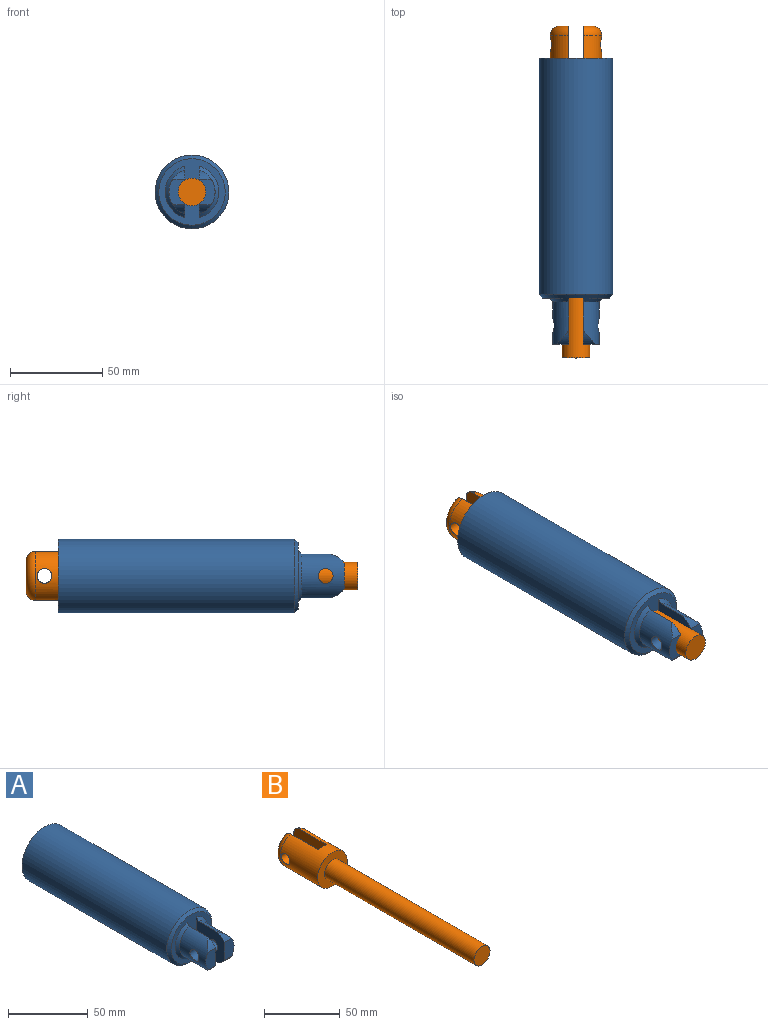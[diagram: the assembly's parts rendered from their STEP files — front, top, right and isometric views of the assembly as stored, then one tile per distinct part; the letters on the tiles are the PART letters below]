
ASSEMBLY  parts=2 mates=1
PART A: 20 faces, bbox 40x155x40 mm
  f0: cylinder r=12.5mm len=23.69mm, axis (0,1,0), area 611mm2, adj f1,f2,f12,f14,f18,f19
  f1: plane 27.92x25.05mm, normal (-1,0,0), area 519mm2, adj f0,f2,f6,f12,f14,f18,f19
  f2: plane 13.64x8.5mm, normal (0,-1,0), area 107mm2, adj f0,f1,f18,f19
  f3: plane 27.92x25.05mm, normal (1,0,0), area 519mm2, adj f4,f5,f6,f11,f13,f16,f17
  f4: cylinder r=12.5mm len=23.69mm, axis (0,1,0), area 610.9mm2, adj f3,f5,f11,f13,f16,f17
  f5: plane 13.64x8.5mm, normal (0,-1,0), area 107mm2, adj f3,f4,f16,f17
  f6: plane 36x36mm, normal (0,-1,0), area 586.4mm2, adj f1,f3,f13,f14,f15
  f7: cylinder r=7.5mm len=120mm, axis (0,1,0), area 5654.9mm2, adj f9,f10
  f8: cylinder r=20mm len=128mm, axis (0,1,0), area 16085mm2, adj f9,f15
  f9: plane 40x40mm, normal (0,1,0), area 1079.9mm2, adj f7,f8
  f10: plane 15x15mm, normal (0,1,0), area 176.7mm2, adj f7
  f11: cylinder r=4mm len=8.5mm, axis (1,0,0), area 205.4mm2, adj f3,f4
  f12: cylinder r=4mm len=8.5mm, axis (1,0,0), area 205.4mm2, adj f0,f1
  f13: cone r=12.5mm half-angle=45deg, axis (0,1,0), area 96.9mm2, adj f3,f4,f6
  f14: cone r=12.5mm half-angle=45deg, axis (0,1,0), area 96.9mm2, adj f0,f1,f6
  f15: cone r=18mm half-angle=45deg, axis (0,1,0), area 337.7mm2, adj f6,f8
  f16: cylinder r=12.1mm len=7.5mm, axis (1,0,0), area 31mm2, adj f3,f4,f5
  f17: cylinder r=12.1mm len=7.5mm, axis (1,0,0), area 31mm2, adj f3,f4,f5
  f18: cylinder r=12.1mm len=7.5mm, axis (1,0,0), area 31mm2, adj f0,f1,f2
  f19: cylinder r=12.1mm len=7.5mm, axis (1,0,0), area 31mm2, adj f0,f1,f2
PART B: 13 faces, bbox 30x180x28.7 mm
  f0: plane 15.82x4.86mm, normal (0,1,0), area 55mm2, adj f2,f9
  f1: cylinder r=13.86mm len=35mm, axis (0,1,0), area 2525.8mm2, adj f2,f6,f7,f8,f9,f10,f11,f12
  f2: torus R=8.86mm, axis (0,-1,0), area 233.1mm2, adj f0,f1,f9
  f3: cylinder r=7.5mm len=140mm, axis (0,-1,0), area 6597.3mm2, adj f4,f6
  f4: plane 15x15mm, normal (0,-1,0), area 176.7mm2, adj f3
  f5: plane 15.82x4.86mm, normal (0,1,0), area 55mm2, adj f7,f10
  f6: plane 27.72x27.72mm, normal (0,-1,0), area 427mm2, adj f1,f3
  f7: torus R=8.86mm, axis (0,-1,0), area 233.1mm2, adj f1,f5,f10
  f8: cylinder r=25mm len=27.73mm, axis (1,0,0), area 231.4mm2, adj f1,f9,f10
  f9: plane 35x26.55mm, normal (1,0,0), area 834.9mm2, adj f0,f1,f2,f8,f12
  f10: plane 35x26.55mm, normal (-1,0,0), area 834.9mm2, adj f1,f5,f7,f8,f11
  f11: cylinder r=4mm len=9.86mm, axis (1,0,0), area 240.5mm2, adj f1,f10
  f12: cylinder r=4mm len=9.86mm, axis (1,0,0), area 240.5mm2, adj f1,f9
PLACE A at identity fixed
PLACE B rot(axis=(0,1,0),180deg) t=(0,-102.5,0)mm
MATE slider B.f3 <-> A.f8  axis (0,-1,0) through (0,-32.5,0)mm
